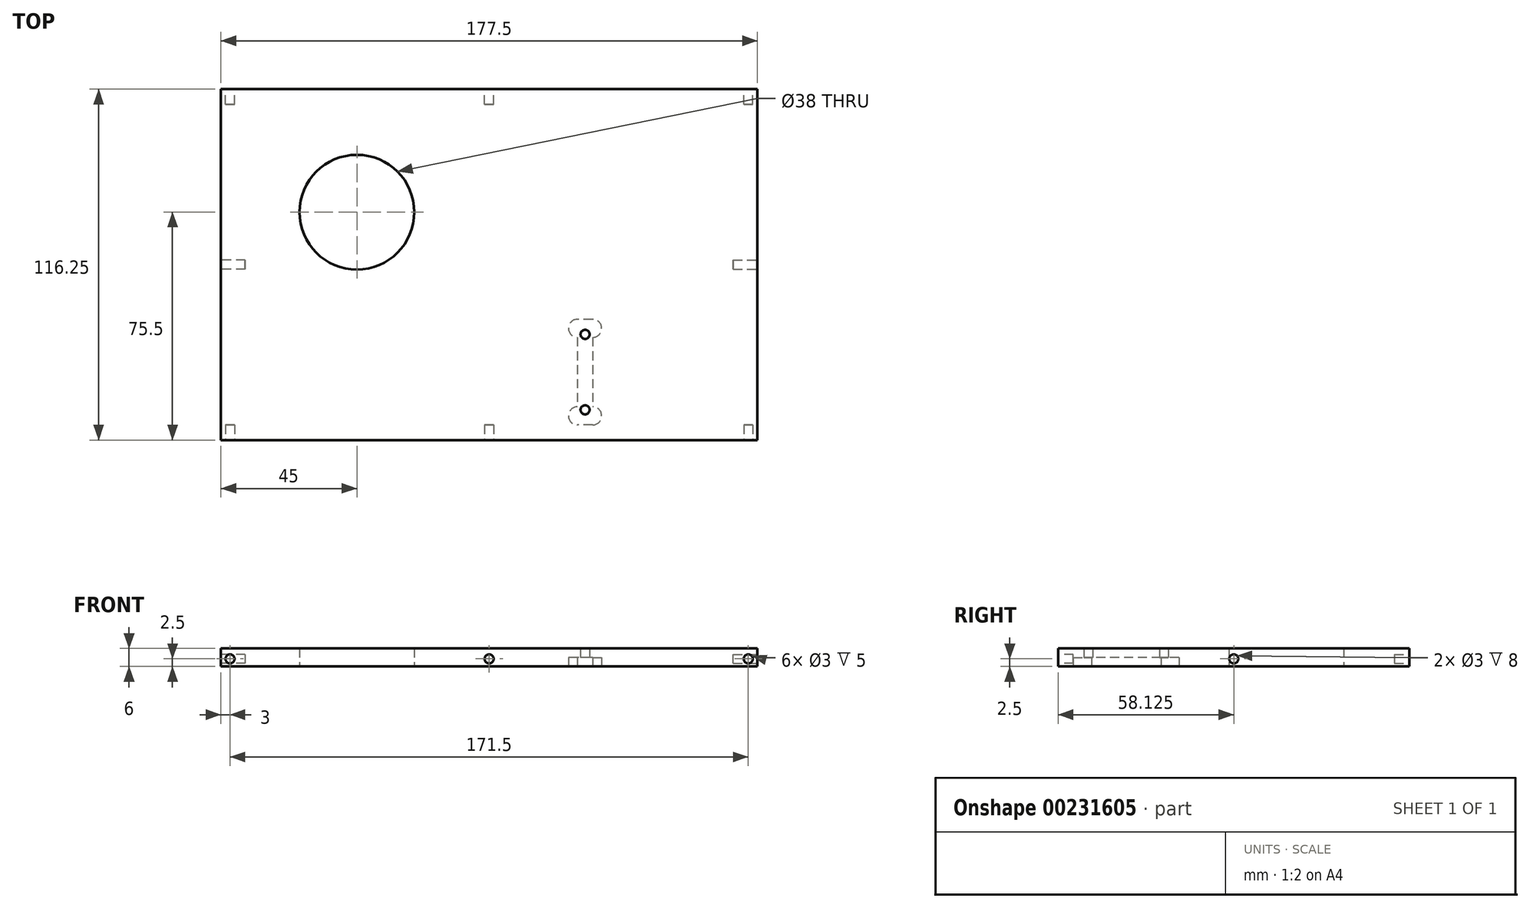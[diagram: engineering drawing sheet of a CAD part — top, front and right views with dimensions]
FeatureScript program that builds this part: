
annotation { "Feature Type Name" : "Feature", "Feature Type Description" : "" }
export const myFeature = defineFeature(function(context is Context, id is Id, definition is map)
    precondition{}
    {
        {
            var Q0;
            Q0=qCreatedBy(makeId("Top.planeOp"),FACE);
            var sketch = newSketch(context, id + "F0", { "sketchPlane" : qUnion([Q0])});
            skLineSegment(sketch, "E0.bottom", {"start": v(0, 0) * mm, "end": v(177.5, 0) * mm});
            skLineSegment(sketch, "E0.top", {"start": v(0, 116.25) * mm, "end": v(177.5, 116.25) * mm});
            skLineSegment(sketch, "E0.left", {"start": v(0, 0) * mm, "end": v(0, 116.25) * mm});
            skLineSegment(sketch, "E0.right", {"start": v(177.5, 0) * mm, "end": v(177.5, 116.25) * mm});
            skLineSegment(sketch, "E1.right", {"start": v(177.5, 40) * mm, "end": v(177.5, 5) * mm});
            skPoint(sketch, "E2.centerSnap1", {"position": v(191.5, -16.13) * mm});
            skPoint(sketch, "E3", {"position": v(177.5, 22.5) * mm});
            skCircle(sketch, "E4", {"center": v(45, 75.5) * mm, "radius": 19 * mm});
            skPoint(sketch, "E5", {"position": v(177.5, 58.12) * mm});
            skLineSegment(sketch, "E6.left", {"start": v(177.5, 64.12) * mm, "end": v(177.5, 52.13) * mm});
            skCircle(sketch, "E7", {"center": v(120.5, 10) * mm, "radius": 1.5 * mm});
            skCircle(sketch, "E8", {"center": v(120.5, 35) * mm, "radius": 1.5 * mm});
            skPoint(sketch, "E9", {"position": v(45, 114.25) * mm});
            skPoint(sketch, "E10", {"position": v(6.25, 75.5) * mm});
            skLineSegment(sketch, "E11", {"start": v(123, 34) * mm, "end": v(123, 11) * mm});
            skLineSegment(sketch, "E12", {"start": v(123, 40) * mm, "end": v(118, 40) * mm});
            skLineSegment(sketch, "E13", {"start": v(123, 5) * mm, "end": v(118, 5) * mm});
            skLineSegment(sketch, "E14", {"start": v(120.5, 5) * mm, "end": v(120.5, 40) * mm, "construction": true});
            skLineSegment(sketch, "E15.trimOffspring", {"start": v(118, 34) * mm, "end": v(118, 11) * mm});
            skArc(sketch, "E16", {"start": v(118, 40) * mm, "mid": v(115, 37) * mm, "end": v(118, 34) * mm});
            skArc(sketch, "E17", {"start": v(118, 11) * mm, "mid": v(115, 8) * mm, "end": v(118, 5) * mm});
            skArc(sketch, "E18", {"start": v(123, 34) * mm, "mid": v(126, 37) * mm, "end": v(123, 40) * mm});
            skArc(sketch, "E19", {"start": v(123, 5) * mm, "mid": v(126, 8) * mm, "end": v(123, 11) * mm});
            skSolve(sketch);
        }
        {
            var Q0;
            Q0=makeQuery(id+"F0.imprint","IMPRINT",FACE,{"disambiguationData":[TD([[makeQuery(id+"F0.imprint","IMPRINT",EDGE,{"derivedFrom":sQuery(id+"F0.wireOp",EDGE,"E0.bottom")}),1.0]])]});
            var Q1;
            Q1=makeQuery(id+"F0.imprint","IMPRINT",FACE,{"disambiguationData":[TD([[makeQuery(id+"F0.imprint","IMPRINT",EDGE,{"derivedFrom":sQuery(id+"F0.wireOp",EDGE,"E2")}),-1.0]])]});
            var Q2;
            {var subQ13=sQuery(id+"F0.wireOp",EDGE,"E0.top");Q2=makeQuery(id+"F0.imprint","IMPRINT",FACE,{"disambiguationData":[TD([[makeQuery(id+"F0.imprint","IMPRINT",EDGE,{"derivedFrom":subQ13}),-1.0]])]});}
            extrude(context, id + "F1", {"entities" : qUnion([Q0, Q1, Q2]), "depth" : 6 * mm});
        }
        {
            var Q0;
            Q0=makeQuery(id+"F0.imprint","IMPRINT",FACE,{"disambiguationData":[TD([[makeQuery(id+"F0.imprint","IMPRINT",EDGE,{"derivedFrom":sQuery(id+"F0.wireOp",EDGE,"E7")}),-1.0]])]});
            extrude(context, id + "F2", {"entities" : qUnion([Q0]), "operationType" : NewBodyOperationType.ADD, "depth" : 6 * mm, "hasSecondDirection" : true, "secondDirectionOppositeDirection" : false, "secondDirectionDepth" : 3 * mm});
        }
        {
            var Q0;
            {var subQ0=sQuery(id+"F0.wireOp",EDGE,"E0.right");Q0=makeQuery(id+"F1.opExtrude","SWEPT_FACE",FACE,{"disambiguationData":[OSD([subQ0]),TDD([makeQuery(id+"F0.imprint","IMPRINT",EDGE,{"disambiguationData":[TD([[makeQuery(id+"F0.imprint","INTERSECT",VERTEX,{"derivedFrom":[sQuery(id+"F0.wireOp",EDGE,"E0.top"),subQ0]}),1.0]])],"derivedFrom":subQ0})])]});}
            var sketch = newSketch(context, id + "F3", { "sketchPlane" : qUnion([Q0])});
            skLineSegment(sketch, "E20", {"start": v(0, 2.5) * mm, "end": v(116.25, 2.5) * mm, "construction": true});
            skCircle(sketch, "E21", {"center": v(58.12, 2.5) * mm, "radius": 1.5 * mm});
            skSolve(sketch);
        }
        {
            var Q0;
            Q0=qSketchRegion(id+"F3",true);
            extrude(context, id + "F4", {"entities" : qUnion([Q0]), "operationType" : NewBodyOperationType.REMOVE, "oppositeDirection" : true, "depth" : 8 * mm});
        }
        {
            var Q0;
            {var subQ0=sQuery(id+"F0.wireOp",EDGE,"f2VROT00-CQCp-64yB-Rn0c-FzvVXhTRJahN.left");var subQ1=sQuery(id+"F0.wireOp",EDGE,"E0.left");Q0=makeQuery(id+"FPQ8oMLjFd6iY3U_1.boolean.opBoolean","MERGE",FACE,{"derivedFrom":[makeQuery(id+"F1.opExtrude","SWEPT_FACE",FACE,{"disambiguationData":[OSD([subQ1]),TDD([makeQuery(id+"F0.imprint","IMPRINT",EDGE,{"disambiguationData":[TD([[makeQuery(id+"F0.imprint","INTERSECT",VERTEX,{"derivedFrom":[sQuery(id+"F0.wireOp",EDGE,"E0.bottom"),subQ1]}),-1.0]])],"derivedFrom":subQ1})])]}),makeQuery(id+"F1.opExtrude","SWEPT_FACE",FACE,{"disambiguationData":[OSD([subQ1]),TDD([makeQuery(id+"F0.imprint","IMPRINT",EDGE,{"disambiguationData":[TD([[makeQuery(id+"F0.imprint","INTERSECT",VERTEX,{"derivedFrom":[sQuery(id+"F0.wireOp",EDGE,"E0.top"),subQ1]}),1.0]])],"derivedFrom":subQ1})])]}),makeQuery(id+"FPQ8oMLjFd6iY3U_1.opExtrude","SWEPT_FACE",FACE,{"disambiguationData":[OSD([subQ0])]})]});}
            var sketch = newSketch(context, id + "F5", { "sketchPlane" : qUnion([Q0])});
            skLineSegment(sketch, "E22", {"start": v(-116.25, 2.5) * mm, "end": v(0, 2.5) * mm, "construction": true});
            skCircle(sketch, "E23", {"center": v(-58.12, 2.5) * mm, "radius": 1.5 * mm});
            skSolve(sketch);
        }
        {
            var Q0;
            Q0=qSketchRegion(id+"F5",true);
            extrude(context, id + "F6", {"entities" : qUnion([Q0]), "operationType" : NewBodyOperationType.REMOVE, "oppositeDirection" : true, "depth" : 8 * mm});
        }
        {
            var Q0;
            Q0=makeQuery(id+"F1.opExtrude","SWEPT_FACE",FACE,{"disambiguationData":[OSD([sQuery(id+"F0.wireOp",EDGE,"E0.bottom")])]});
            var sketch = newSketch(context, id + "F7", { "sketchPlane" : qUnion([Q0])});
            skLineSegment(sketch, "E24", {"start": v(0, 2.5) * mm, "end": v(177.5, 2.5) * mm, "construction": true});
            skCircle(sketch, "E25", {"center": v(3, 2.5) * mm, "radius": 1.5 * mm});
            skCircle(sketch, "E26", {"center": v(88.75, 2.5) * mm, "radius": 1.5 * mm});
            skCircle(sketch, "E27", {"center": v(174.5, 2.5) * mm, "radius": 1.5 * mm});
            skSolve(sketch);
        }
        {
            var Q0;
            Q0=qSketchRegion(id+"F7",true);
            extrude(context, id + "F8", {"entities" : qUnion([Q0]), "operationType" : NewBodyOperationType.REMOVE, "oppositeDirection" : true, "depth" : 5 * mm});
        }
        {
            var Q0;
            Q0=makeQuery(id+"F1.opExtrude","SWEPT_FACE",FACE,{"disambiguationData":[OSD([sQuery(id+"F0.wireOp",EDGE,"E0.top")])]});
            var sketch = newSketch(context, id + "F9", { "sketchPlane" : qUnion([Q0])});
            skLineSegment(sketch, "E28", {"start": v(-177.5, 2.5) * mm, "end": v(0, 2.5) * mm, "construction": true});
            skCircle(sketch, "E29", {"center": v(-3, 2.5) * mm, "radius": 1.5 * mm});
            skCircle(sketch, "E30", {"center": v(-88.75, 2.5) * mm, "radius": 1.5 * mm});
            skCircle(sketch, "E31", {"center": v(-174.5, 2.5) * mm, "radius": 1.5 * mm});
            skSolve(sketch);
        }
        {
            var Q0;
            Q0=qSketchRegion(id+"F9",true);
            extrude(context, id + "F10", {"entities" : qUnion([Q0]), "operationType" : NewBodyOperationType.REMOVE, "oppositeDirection" : true, "depth" : 5 * mm});
        }
    });
